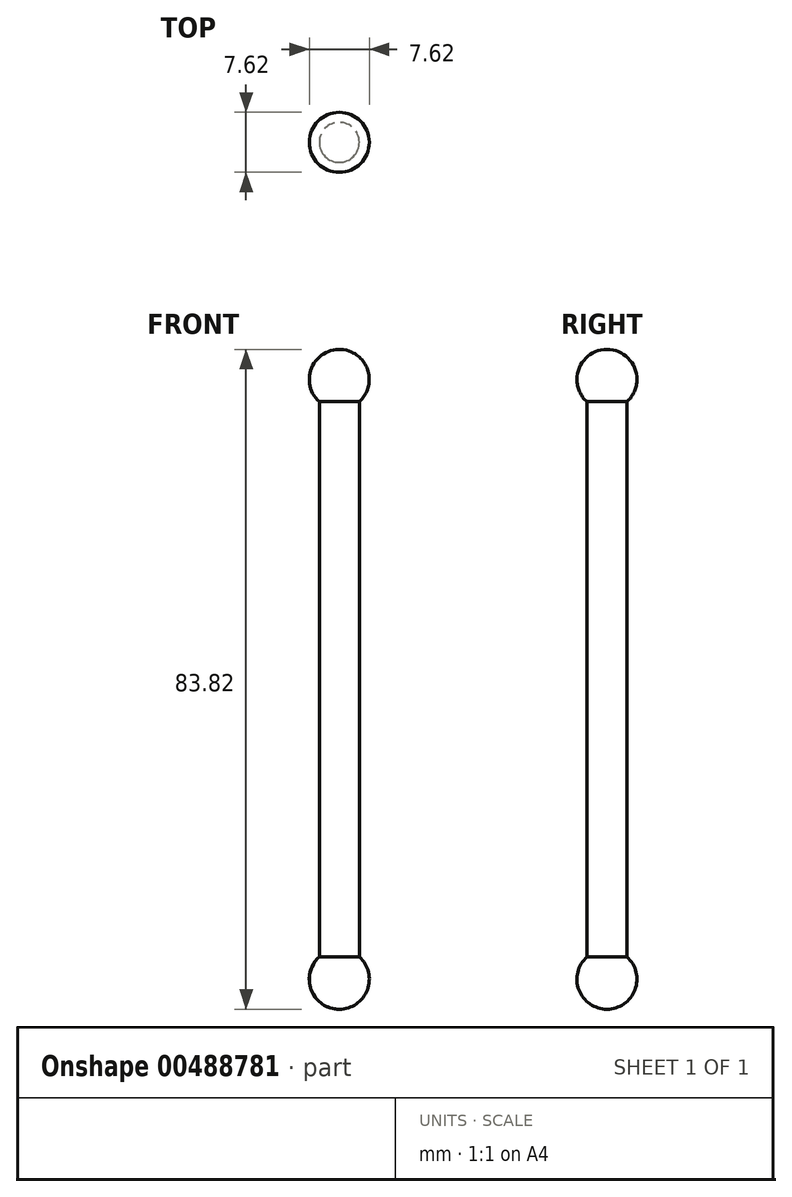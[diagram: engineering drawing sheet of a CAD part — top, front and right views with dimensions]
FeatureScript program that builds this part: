
annotation { "Feature Type Name" : "Feature", "Feature Type Description" : "" }
export const myFeature = defineFeature(function(context is Context, id is Id, definition is map)
    precondition{}
    {
        {
            var Q0;
            Q0=qCreatedBy(makeId("Front.planeOp"),FACE);
            var sketch = newSketch(context, id + "F0", { "sketchPlane" : qUnion([Q0])});
            skArc(sketch, "E0", {"start": v(0, -3.81) * mm, "mid": v(3.81, 0) * mm, "end": v(0, 3.81) * mm});
            skLineSegment(sketch, "E1", {"start": v(0, 3.81) * mm, "end": v(0, -3.81) * mm});
            skSolve(sketch);
        }
        {
            var Q0;
            Q0=makeQuery(id+"F0.imprint","IMPRINT",FACE,{"disambiguationData":[TD([[makeQuery(id+"F0.imprint","IMPRINT",EDGE,{"derivedFrom":sQuery(id+"F0.wireOp",EDGE,"E0")}),1.0]])]});
            var Q1;
            Q1=sQuery(id+"F0.wireOp",EDGE,"E1");
            revolve(context, id + "F1", {"surfaceOperationType" : NewSurfaceOperationType.NEW, "entities" : qUnion([Q0]), "axis" : qUnion([Q1]), "revolveType" : RevolveType.FULL});
        }
        {
            var Q0;
            Q0=qCreatedBy(makeId("Top.planeOp"),FACE);
            var sketch = newSketch(context, id + "F2", { "sketchPlane" : qUnion([Q0])});
            skCircle(sketch, "E2", {"center": v(0, 0) * mm, "radius": 2.54 * mm});
            skSolve(sketch);
        }
        {
            var Q0;
            Q0 = qSketchRegion(id + "F2", true);
            extrude(context, id + "F3", {"entities" : qUnion([Q0]), "operationType" : NewBodyOperationType.ADD, "depth" : 76.2 * mm, "offsetDistance" : 25.4 * mm});
        }
        {
            var Q0;
            Q0=makeQuery(id+"F3.opExtrude","CAP_FACE",FACE,{"disambiguationData":[OSD([sQuery(id+"F2.wireOp",EDGE,"E2")])],"isStart":false});
            var sketch = newSketch(context, id + "F4", { "sketchPlane" : qUnion([Q0])});
            skArc(sketch, "E3", {"start": v(0, -3.81) * mm, "mid": v(3.81, 0) * mm, "end": v(0, 3.81) * mm});
            skLineSegment(sketch, "E4", {"start": v(0, 3.81) * mm, "end": v(0, -3.81) * mm});
            skSolve(sketch);
        }
        {
            var Q0;
            {var subQ0=sQuery(id+"F4.wireOp",EDGE,"E3");Q0=makeQuery(id+"F4.imprint","IMPRINT",FACE,{"disambiguationData":[TD([[makeQuery(id+"F4.imprint","IMPRINT",EDGE,{"derivedFrom":subQ0}),1.0]])]});}
            var Q1;
            {var subQ0=sQuery(id+"F4.wireOp",EDGE,"E4");var subQ1=makeQuery(id+"F3.opExtrude","CAP_EDGE",EDGE,{"disambiguationData":[OSD([sQuery(id+"F2.wireOp",EDGE,"E2")])],"isStart":false});var subQ2=makeQuery(id+"F4.imprint","INTERSECT",VERTEX,{"disambiguationData":[OD(0.0)],"derivedFrom":[subQ1,subQ0]});Q1=makeQuery(id+"F4.imprint","IMPRINT",FACE,{"disambiguationData":[TD([[makeQuery(id+"F4.imprint","IMPRINT",EDGE,{"disambiguationData":[TD([[subQ2,-1.0]])],"derivedFrom":subQ0}),1.0]])]});}
            var Q2;
            Q2=sQuery(id+"F4.wireOp",EDGE,"E4");
            revolve(context, id + "F5", {"operationType" : NewBodyOperationType.ADD, "surfaceOperationType" : NewSurfaceOperationType.NEW, "entities" : qUnion([Q0, Q1]), "axis" : qUnion([Q2]), "revolveType" : RevolveType.FULL});
        }
    });
